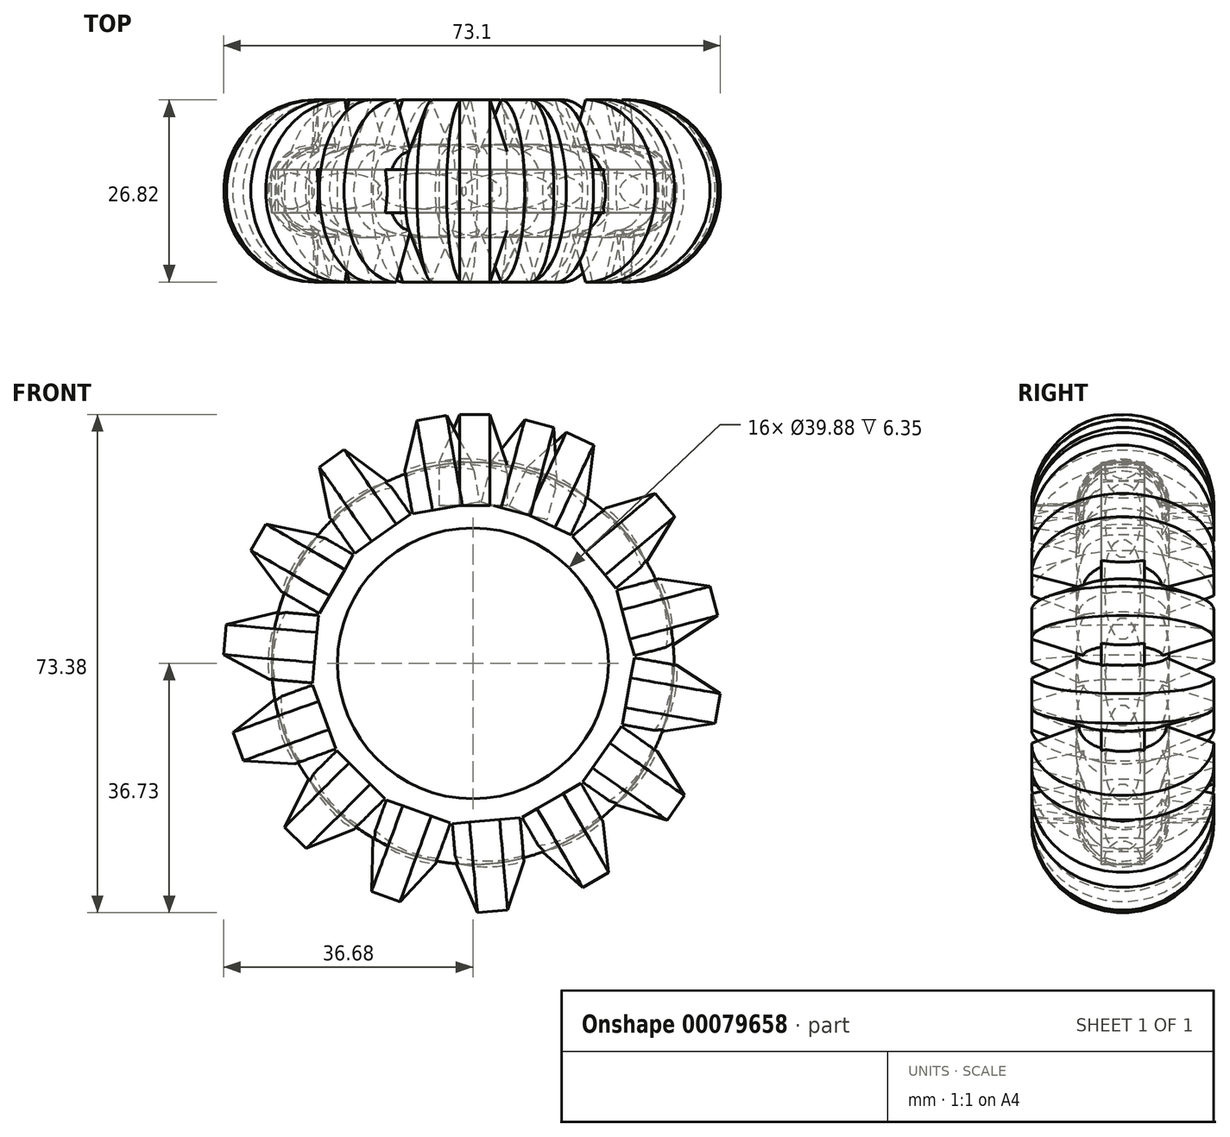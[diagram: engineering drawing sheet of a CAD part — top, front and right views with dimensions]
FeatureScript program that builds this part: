
annotation { "Feature Type Name" : "Feature", "Feature Type Description" : "" }
export const myFeature = defineFeature(function(context is Context, id is Id, definition is map)
    precondition{}
    {
        {
            var Q0;
            Q0=qCreatedBy(makeId("Front.planeOp"),FACE);
            var sketch = newSketch(context, id + "F0", { "sketchPlane" : qUnion([Q0])});
            skCircle(sketch, "E0", {"center": v(0, 0) * mm, "radius": 29.6 * mm});
            skCircle(sketch, "E1", {"center": v(0, 0) * mm, "radius": 19.94 * mm});
            skSolve(sketch);
        }
        {
            var Q0;
            Q0=makeQuery(id+"F0.imprint","IMPRINT",FACE,{"disambiguationData":[TD([[makeQuery(id+"F0.imprint","IMPRINT",EDGE,{"derivedFrom":sQuery(id+"F0.wireOp",EDGE,"E0")}),1.0]])]});
            extrude(context, id + "F1", {"entities" : qUnion([Q0]), "depth" : 3.17 * mm, "hasSecondDirection" : true, "secondDirectionOppositeDirection" : true, "secondDirectionDepth" : 3.17 * mm});
        }
        {
            var Q0;
            Q0=qCreatedBy(makeId("Front.planeOp"),FACE);
            var sketch = newSketch(context, id + "F2", { "sketchPlane" : qUnion([Q0])});
            skLineSegment(sketch, "E2", {"start": v(-4.94, 29.66) * mm, "end": v(-1.92, 36.65) * mm});
            skLineSegment(sketch, "E3", {"start": v(-1.92, 36.65) * mm, "end": v(2.53, 36.65) * mm});
            skLineSegment(sketch, "E4", {"start": v(2.53, 36.65) * mm, "end": v(5.07, 29.03) * mm});
            skArc(sketch, "E5", {"start": v(5.07, 29.03) * mm, "mid": v(0.11, 30.06) * mm, "end": v(-4.94, 29.66) * mm});
            skLineSegment(sketch, "E6", {"start": v(-23.93, 23.24) * mm, "end": v(28.47, 23.24) * mm, "construction": true});
            skSolve(sketch);
        }
        {
            var Q0;
            Q0=makeQuery(id+"F2.imprint","IMPRINT",FACE,{"disambiguationData":[TD([[makeQuery(id+"F2.imprint","IMPRINT",EDGE,{"derivedFrom":sQuery(id+"F2.wireOp",EDGE,"E2")}),-1.0]])]});
            var Q1;
            Q1=sQuery(id+"F2.wireOp",EDGE,"E6");
            var Q2;
            Q2=sQuery(id+"F2.wireOp",EDGE,"E6");
            revolve(context, id + "F3", {"operationType" : NewBodyOperationType.ADD, "entities" : qUnion([Q0]), "surfaceEntities" : qUnion([Q1]), "axis" : qUnion([Q2]), "revolveType" : RevolveType.SYMMETRIC, "angle" : 180 * degree});
        }
        {
            var Q0;
            Q0=makeQuery(id+"F1.opExtrude","SWEPT_BODY",BODY,{"disambiguationData":[OSD([sQuery(id+"F0.wireOp",EDGE,"E0"),sQuery(id+"F0.wireOp",EDGE,"E1")])]});
            var Q1;
            Q1=makeQuery(id+"F1.opExtrude","SWEPT_FACE",FACE,{"disambiguationData":[OSD([sQuery(id+"F0.wireOp",EDGE,"E0")])]});
            circularPattern(context, id + "F4", {"entities" : qUnion([Q0]), "axis" : qUnion([Q1]), "angle" : 25 * degree, "instanceCount" : 16, "computeTransformsWithoutBuiltin" : true});
        }
    });
